# Revit family: QF_HOSHIZAKI_IM-30CWNE
name_source: partatom
category: Specialty Equipment
revit_build: Autodesk Revit 2016 (Build: 20150220_1215(x64)
units: mm (PartAtom-declared; Revit-internal decimal feet)

## family parameters
Always vertical = Yes
Cut with Voids When Loaded = No
OmniClass Number = 23.40.40.14
OmniClass Title = Food Service Equipment
Part Type = Normal
Room Calculation Point = No
Round Connector Dimension = Use Diameter
Shared = No
Work Plane-Based = No

## types (2) — shared parameters
Accessory = No
Apparent Power = 270 VA
Assembly Code = E1090320
Cold Water Flow = 0.0 L/s
Cold Water Size = 19 mm
Cold Water Temperature Recommended = 0 °C
Conn Conduit = No
Depth Actual = 451 mm  [stored 1.47966 ft]
Description = SELF CONTAINED IM ICE MAKER, 30KG PER 24 HOURS, LARGE CUBE, LOW COUNTER, WATER COOLED
Electric power = 270 W
FL Amps = 20 A
Height Actual = 695 mm  [stored 2.28018 ft]
Indirect Waste Size = 19 mm
Length Actual = 398 mm  [stored 1.30577 ft]
Manufacturer = HOSHIZAKI
Max Overcurrent Protection = 0 A
Min Ckt Ampacity = 0 A
Model = IM-30CWNE
Number of Poles = 2
Phase = 1
URL = www.hoshizaki-europe.com
Weight = 34.00 kg
zero-valued in all types: Cost

## per-type parameters (varying)
| type | Cycle | Volts |
| IM-30CWNE_230V/1Ph/50Hz | 50 Hz | 230 V |
| IM-30CWNE_240V/1Ph/60Hz | 60 Hz | 240 V |

note: [stored X ft] marks values corroborated as IEEE doubles in the binary element streams (Revit-internal decimal feet)

## geometry (parser evidence)
native form markers: Blend x2, Sweep x4
no freeform markers — native parametric forms only
